# Revit family: VentAxia_Commercial_EC_SlimpakBoxFan_1
name_source: partatom
category: Mechanical Equipment
units: mm (PartAtom-declared; Revit-internal decimal feet)

## family parameters
Always vertical = Yes
Cut with Voids When Loaded = No
OmniClass Number = 23.75.70.00
OmniClass Title = HVAC Distribution Devices
Part Type = Normal
Room Calculation Point = No
Round Connector Dimension = Use Diameter
Shared = No
Work Plane-Based = No

## types (8) — shared parameters
Assembly Code = D3040100
AssetType = Fixed
BIMObjectName = VentAxia_Commercial_EC_SlimpakBoxFan
ClassificationName = Uniclass2015
ClassificationValue = Pr_65_67_29
CodePerformance = ‘O’ class rated, BS476 part 6 & 7
Color = Light Grey
Description = The New range of Slimpak EC single in-line box fans incorporate an energy efficient EC motor and basic commissioning controls to offer an energy efficient basic fan system.
DocumentationCertificates = https://www.vent-axia.com
DocumentationInstallationGuide = https://www.vent-axia.com
DocumentationLiterature = https://www.vent-axia.com
DocumentationMaintenance = https://www.vent-axia.com
DocumentationTechnical = https://www.vent-axia.com
DurationUnit = Years
Finish = Galvanised
IfcExportAs = IfcAirTerminal
IfcExportType = IfcAirTerminalTypeEnum.DIFFUSER
Keynote = U10/110
Manufacturer = Vent-Axia Limited
ManufacturerName = Vent-Axia Limited
Material = Steel
ModelReference = Slimpak EC Box Fan
NBSDescription = Overhead ventilators
NBSObjectName = Vent-Axia - Fans
ProductionYear = 2024
ReferencedStandard = BS EN ISO 9001:1994.
Shape = Rectangle
Type Comments = Slimpak EC Box Fan
URL = https://www.vent-axia.com
UnitMaterial = Vent-Axia - Steel - Galvanised - Grey
WarrantyDurationLabor = 0
WarrantyDurationParts = 0
WarrantyDurationUnit = Years
_BSBibleVersion = 17
_CurrentRevision = 1
_DistributedBy = https://www.bimstore.co
_ObjectUserGuide = https://www.vent-axia.com
zero-valued in all types: Default Elevation, ExpectedLife, Offset, _BimSpecGuid

## per-type parameters (varying)
| type | NominalDepth | NominalHeight | NominalLength | Size | TypeName | UnitHeight | UnitLength | UnitWidth | a | b | c | d | e | f | g | h | i |
| SLP100EC | 310 mm  [stored 1.01706 ft] | 192 mm  [stored 0.629921 ft] | 456 mm  [stored 1.49606 ft] | 456x310x192mm | Slimpak EC Box Fan - SLP100EC | 192 mm  [stored 0.629921 ft] | 456 mm  [stored 1.49606 ft] | 310 mm  [stored 1.01706 ft] | 100 mm  [stored 0.328084 ft] | 380 mm | 275 mm | 456 mm  [stored 1.49606 ft] | 310 mm  [stored 1.01706 ft] | 192 mm  [stored 0.629921 ft] | 155 mm  [stored 0.50853 ft] | 93 mm  [stored 0.305118 ft] | 96 mm  [stored 0.314961 ft] |
| SLP500EC | 770 mm | 577 mm | 975 mm | 975x770x577mm | Slimpak EC Box Fan - SLP500EC | 577 mm | 975 mm | 770 mm | 500 mm | 898 mm | 735 mm | 975 mm | 770 mm | 577 mm | 385 mm | 326 mm | 286 mm |
| SLP400EC | 572 mm | 460 mm | 785 mm | 785x572x460mm | Slimpak EC Box Fan - SLP400EC | 460 mm | 785 mm | 572 mm | 400 mm | 710 mm | 540 mm | 785 mm | 572 mm | 460 mm | 286 mm | 243 mm | 230 mm |
| SLP315EC | 572 mm | 460 mm | 785 mm | 785x572x460mm | Slimpak EC Box Fan - SLP315EC | 460 mm | 785 mm | 572 mm | 315 mm | 710 mm | 540 mm | 785 mm | 572 mm | 460 mm | 286 mm | 243 mm | 230 mm |
| SLP250EC | 364 mm | 287 mm | 511 mm | 511x364x287mm | Slimpak EC Box Fan - SLP250EC | 287 mm | 511 mm | 364 mm | 250 mm | 435 mm | 330 mm | 511 mm | 364 mm | 287 mm | 182 mm | 147 mm | 143 mm |
| SLP200EC | 364 mm | 287 mm | 511 mm | 511x364x287mm | Slimpak EC Box Fan - SLP200EC | 287 mm | 511 mm | 364 mm | 200 mm | 435 mm | 330 mm | 511 mm | 364 mm | 287 mm | 182 mm | 122 mm | 143 mm |
| SLP150EC | 310 mm  [stored 1.01706 ft] | 192 mm  [stored 0.629921 ft] | 456 mm  [stored 1.49606 ft] | 456x310x192mm | Slimpak EC Box Fan - SLP150EC | 192 mm  [stored 0.629921 ft] | 456 mm  [stored 1.49606 ft] | 310 mm  [stored 1.01706 ft] | 150 mm | 380 mm | 275 mm | 456 mm  [stored 1.49606 ft] | 310 mm  [stored 1.01706 ft] | 192 mm  [stored 0.629921 ft] | 155 mm  [stored 0.50853 ft] | 108 mm | 96 mm  [stored 0.314961 ft] |
| SLP125EC | 310 mm  [stored 1.01706 ft] | 192 mm  [stored 0.629921 ft] | 456 mm  [stored 1.49606 ft] | 456x310x192mm | Slimpak EC Box Fan - SLP125EC | 192 mm  [stored 0.629921 ft] | 456 mm  [stored 1.49606 ft] | 310 mm  [stored 1.01706 ft] | 125 mm | 380 mm | 275 mm | 456 mm  [stored 1.49606 ft] | 310 mm  [stored 1.01706 ft] | 192 mm  [stored 0.629921 ft] | 155 mm  [stored 0.50853 ft] | 108 mm | 96 mm  [stored 0.314961 ft] |

note: column(s) folded — value = type name in every type: Model, ModelNumber

note: [stored X ft] marks values corroborated as IEEE doubles in the binary element streams (Revit-internal decimal feet)

## geometry (parser evidence)
native form markers: Blend x4, Sweep x2
no freeform markers — native parametric forms only
